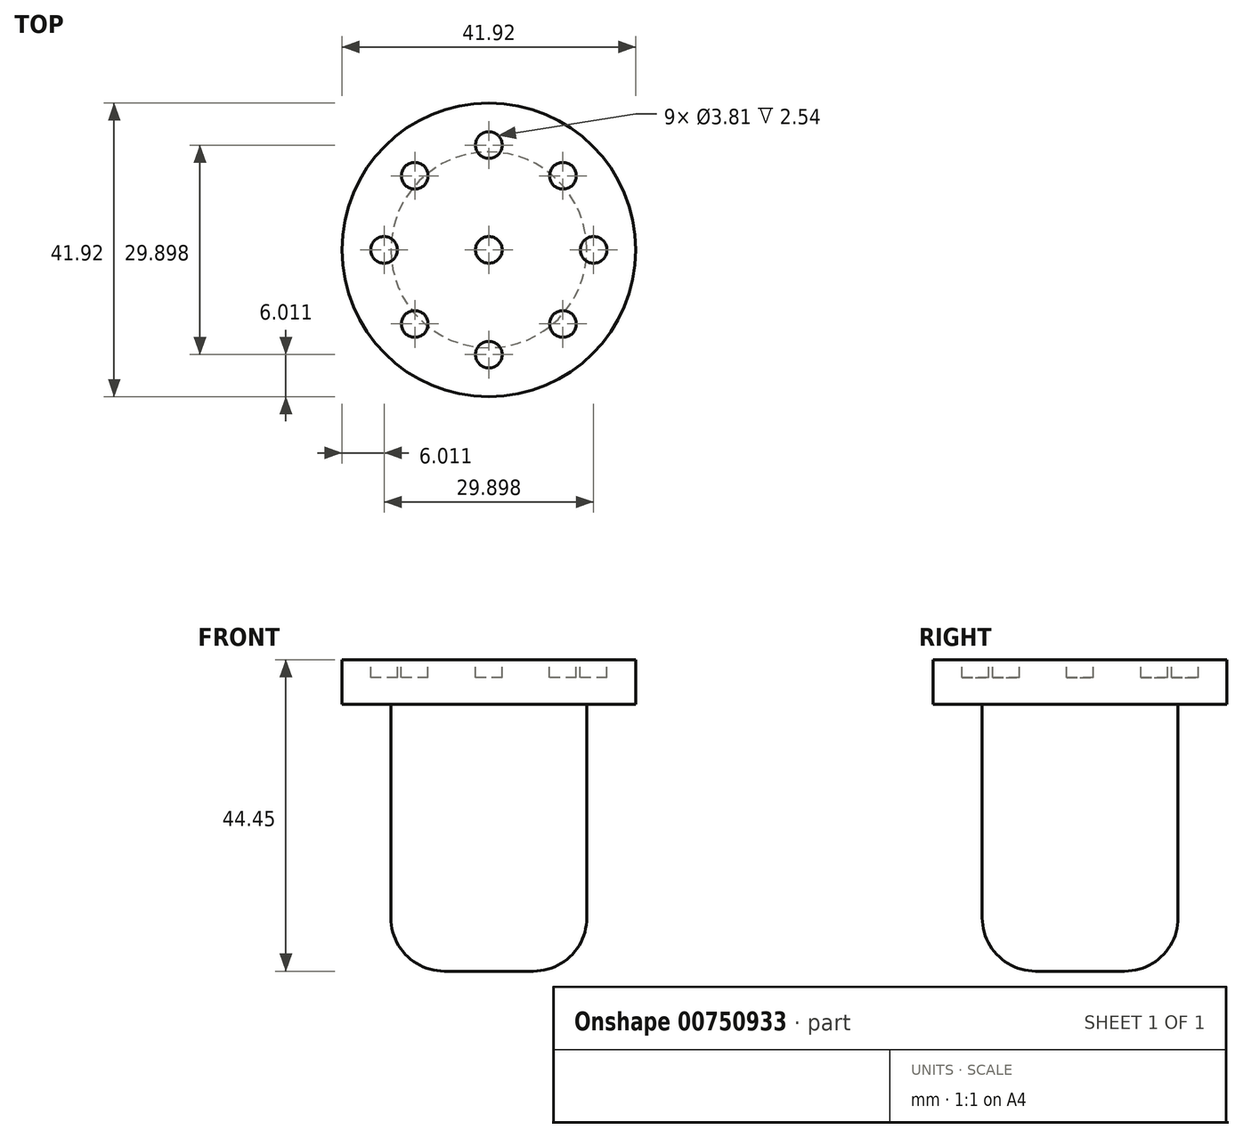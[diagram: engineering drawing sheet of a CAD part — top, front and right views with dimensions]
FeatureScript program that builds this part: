
annotation { "Feature Type Name" : "Feature", "Feature Type Description" : "" }
export const myFeature = defineFeature(function(context is Context, id is Id, definition is map)
    precondition{}
    {
        {
            var Q0;
            Q0=qCreatedBy(makeId("Top.planeOp"),FACE);
            var sketch = newSketch(context, id + "F0", { "sketchPlane" : qUnion([Q0])});
            skCircle(sketch, "E0", {"center": v(0, 0) * mm, "radius": 20.96 * mm});
            skSolve(sketch);
        }
        {
            var Q0;
            Q0=makeQuery(id+"F0.imprint","IMPRINT",FACE,{"disambiguationData":[TD([[makeQuery(id+"F0.imprint","IMPRINT",EDGE,{"derivedFrom":sQuery(id+"F0.wireOp",EDGE,"E0")}),1.0]])]});
            extrude(context, id + "F1", {"entities" : qUnion([Q0]), "depth" : 6.35 * mm, "offsetDistance" : 25.4 * mm});
        }
        {
            var Q0;
            Q0=makeQuery(id+"F1.opExtrude","CAP_FACE",FACE,{"disambiguationData":[OSD([sQuery(id+"F0.wireOp",EDGE,"E0")])],"isStart":false});
            var sketch = newSketch(context, id + "F2", { "sketchPlane" : qUnion([Q0])});
            skCircle(sketch, "E1", {"center": v(0, 14.95) * mm, "radius": 1.9 * mm});
            skPoint(sketch, "E2.center", {"position": v(0, 0) * mm});
            skLineSegment(sketch, "E2.anchor1", {"start": v(0, 0) * mm, "end": v(0, 14.95) * mm, "construction": true});
            skCircle(sketch, "E3.1.0", {"center": v(10.57, 10.57) * mm, "radius": 1.9 * mm});
            skCircle(sketch, "E3.2.0", {"center": v(14.95, 0) * mm, "radius": 1.9 * mm});
            skLineSegment(sketch, "E3.anchor2", {"start": v(0, 0) * mm, "end": v(14.95, 0) * mm, "construction": true});
            skCircle(sketch, "E4.1.0", {"center": v(10.57, -10.57) * mm, "radius": 1.9 * mm});
            skCircle(sketch, "E4.2.0", {"center": v(0, -14.95) * mm, "radius": 1.9 * mm});
            skLineSegment(sketch, "E4.anchor2", {"start": v(0, 0) * mm, "end": v(0, -14.95) * mm, "construction": true});
            skCircle(sketch, "E5.1.0", {"center": v(-10.57, -10.57) * mm, "radius": 1.9 * mm});
            skCircle(sketch, "E5.2.0", {"center": v(-14.95, 0) * mm, "radius": 1.9 * mm});
            skLineSegment(sketch, "E5.anchor2", {"start": v(0, 0) * mm, "end": v(-14.95, 0) * mm, "construction": true});
            skCircle(sketch, "E6.1.0", {"center": v(-10.57, 10.57) * mm, "radius": 1.9 * mm});
            skSolve(sketch);
        }
        {
            var Q0;
            Q0=makeQuery(id+"F1.opExtrude","CAP_FACE",FACE,{"disambiguationData":[OSD([sQuery(id+"F0.wireOp",EDGE,"E0")])],"isStart":true});
            var sketch = newSketch(context, id + "F3", { "sketchPlane" : qUnion([Q0])});
            skCircle(sketch, "E7", {"center": v(0, 0) * mm, "radius": 13.97 * mm});
            skSolve(sketch);
        }
        {
            var Q0;
            Q0=makeQuery(id+"F3.imprint","IMPRINT",FACE,{"disambiguationData":[TD([[makeQuery(id+"F3.imprint","IMPRINT",EDGE,{"derivedFrom":sQuery(id+"F3.wireOp",EDGE,"E7")}),1.0]])]});
            extrude(context, id + "F4", {"entities" : qUnion([Q0]), "operationType" : NewBodyOperationType.ADD, "depth" : 38.1 * mm, "offsetDistance" : 25.4 * mm});
        }
        {
            var Q0;
            Q0=makeQuery(id+"F4.opExtrude","CAP_EDGE",EDGE,{"disambiguationData":[OSD([sQuery(id+"F3.wireOp",EDGE,"E7")])],"isStart":false});
            fillet(context, id + "F5", {"entities" : qUnion([Q0]), "radius" : 7.62 * mm, "tangentPropagation" : true, "allowEdgeOverflow" : false});
        }
        {
            var Q0;
            Q0=makeQuery(id+"F2.imprint","IMPRINT",FACE,{"disambiguationData":[TD([[makeQuery(id+"F2.imprint","IMPRINT",EDGE,{"derivedFrom":sQuery(id+"F2.wireOp",EDGE,"E3.1.0")}),-1.0]])]});
            var sketch = newSketch(context, id + "F6", { "sketchPlane" : qUnion([Q0])});
            skCircle(sketch, "E8", {"center": v(0, 0) * mm, "radius": 1.9 * mm});
            skSolve(sketch);
        }
        {
            var Q0;
            Q0=makeQuery(id+"F2.imprint","IMPRINT",FACE,{"disambiguationData":[TD([[makeQuery(id+"F2.imprint","IMPRINT",EDGE,{"derivedFrom":sQuery(id+"F2.wireOp",EDGE,"E4.1.0")}),1.0]])]});
            var Q1;
            Q1=sQuery(id+"F2.wireOp",EDGE,"E4.1.0");
            extrude(context, id + "F7", {"entities" : qUnion([Q0]), "operationType" : NewBodyOperationType.REMOVE, "surfaceEntities" : qUnion([Q1]), "oppositeDirection" : true, "depth" : 2.54 * mm, "offsetDistance" : 25.4 * mm});
        }
        {
            var Q0;
            Q0=makeQuery(id+"F6.imprint","IMPRINT",FACE,{"disambiguationData":[TD([[makeQuery(id+"F6.imprint","IMPRINT",EDGE,{"derivedFrom":makeQuery(id+"F2.imprint","IMPRINT",EDGE,{"derivedFrom":sQuery(id+"F2.wireOp",EDGE,"E5.1.0")})}),1.0]])]});
            var Q1;
            Q1=makeQuery(id+"F6.imprint","IMPRINT",FACE,{"disambiguationData":[TD([[makeQuery(id+"F6.imprint","IMPRINT",EDGE,{"derivedFrom":makeQuery(id+"F2.imprint","IMPRINT",EDGE,{"derivedFrom":sQuery(id+"F2.wireOp",EDGE,"E3.1.0")})}),1.0]])]});
            var Q2;
            Q2=makeQuery(id+"F6.imprint","IMPRINT",FACE,{"disambiguationData":[TD([[makeQuery(id+"F6.imprint","IMPRINT",EDGE,{"derivedFrom":makeQuery(id+"F2.imprint","IMPRINT",EDGE,{"derivedFrom":sQuery(id+"F2.wireOp",EDGE,"E6.1.0")})}),1.0]])]});
            var Q3;
            Q3=makeQuery(id+"F6.imprint","IMPRINT",FACE,{"disambiguationData":[TD([[makeQuery(id+"F6.imprint","IMPRINT",EDGE,{"derivedFrom":sQuery(id+"F6.wireOp",EDGE,"E8")}),1.0]])]});
            var Q4;
            Q4=makeQuery(id+"F6.imprint","IMPRINT",FACE,{"disambiguationData":[TD([[makeQuery(id+"F6.imprint","IMPRINT",EDGE,{"derivedFrom":makeQuery(id+"F2.imprint","IMPRINT",EDGE,{"derivedFrom":sQuery(id+"F2.wireOp",EDGE,"E1")})}),1.0]])]});
            var Q5;
            Q5=makeQuery(id+"F6.imprint","IMPRINT",FACE,{"disambiguationData":[TD([[makeQuery(id+"F6.imprint","IMPRINT",EDGE,{"derivedFrom":makeQuery(id+"F2.imprint","IMPRINT",EDGE,{"derivedFrom":sQuery(id+"F2.wireOp",EDGE,"E3.2.0")})}),1.0]])]});
            var Q6;
            Q6=makeQuery(id+"F6.imprint","IMPRINT",FACE,{"disambiguationData":[TD([[makeQuery(id+"F6.imprint","IMPRINT",EDGE,{"derivedFrom":makeQuery(id+"F2.imprint","IMPRINT",EDGE,{"derivedFrom":sQuery(id+"F2.wireOp",EDGE,"E4.2.0")})}),1.0]])]});
            var Q7;
            Q7=makeQuery(id+"F6.imprint","IMPRINT",FACE,{"disambiguationData":[TD([[makeQuery(id+"F6.imprint","IMPRINT",EDGE,{"derivedFrom":makeQuery(id+"F2.imprint","IMPRINT",EDGE,{"derivedFrom":sQuery(id+"F2.wireOp",EDGE,"E4.1.0")})}),1.0]])]});
            var Q8;
            Q8=makeQuery(id+"F6.imprint","IMPRINT",FACE,{"disambiguationData":[TD([[makeQuery(id+"F6.imprint","IMPRINT",EDGE,{"derivedFrom":makeQuery(id+"F2.imprint","IMPRINT",EDGE,{"derivedFrom":sQuery(id+"F2.wireOp",EDGE,"E5.2.0")})}),1.0]])]});
            extrude(context, id + "F8", {"entities" : qUnion([Q0, Q1, Q2, Q3, Q4, Q5, Q6, Q7, Q8]), "operationType" : NewBodyOperationType.REMOVE, "oppositeDirection" : true, "depth" : 2.54 * mm, "offsetDistance" : 25.4 * mm});
        }
    });
